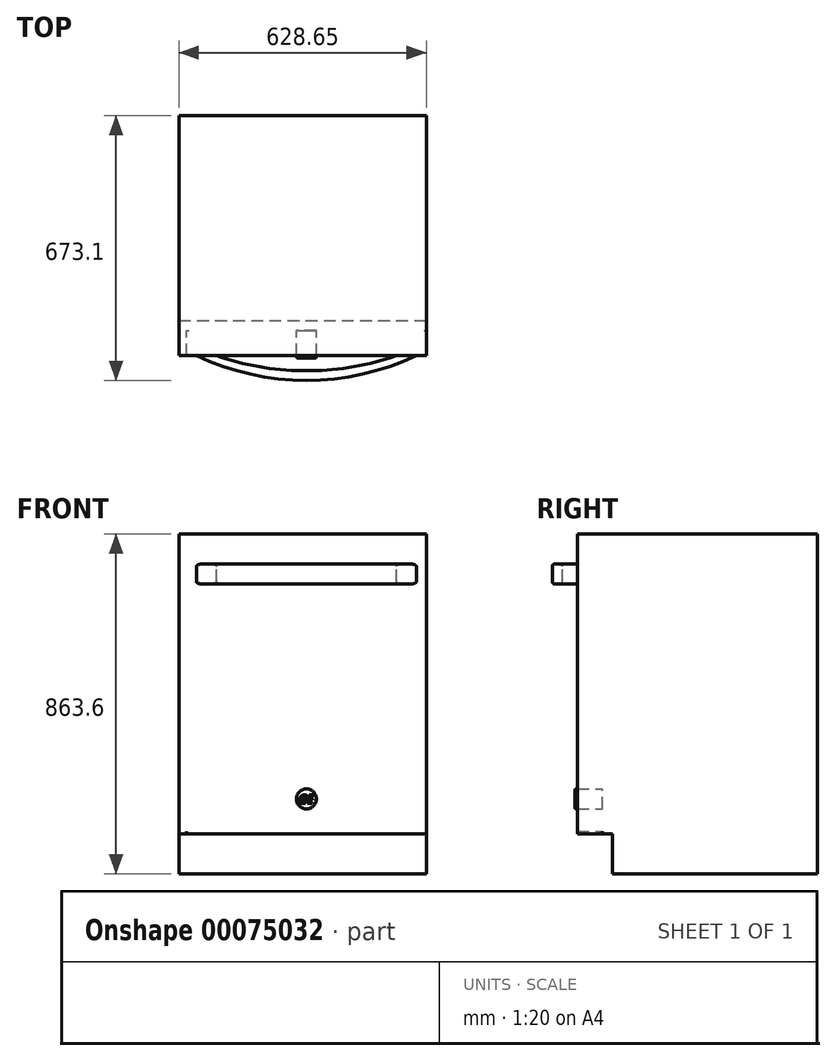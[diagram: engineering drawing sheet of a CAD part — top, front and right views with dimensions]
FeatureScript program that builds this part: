
annotation { "Feature Type Name" : "Feature", "Feature Type Description" : "" }
export const myFeature = defineFeature(function(context is Context, id is Id, definition is map)
    precondition{}
    {
        {
            var Q0;
            Q0=qCreatedBy(makeId("Front.planeOp"),FACE);
            var sketch = newSketch(context, id + "F0", { "sketchPlane" : qUnion([Q0])});
            skLineSegment(sketch, "E0.bottom", {"start": v(-304.8, 431.8) * mm, "end": v(304.8, 431.8) * mm});
            skLineSegment(sketch, "E0.top", {"start": v(-304.8, -431.8) * mm, "end": v(304.8, -431.8) * mm});
            skLineSegment(sketch, "E0.left", {"start": v(-304.8, 431.8) * mm, "end": v(-304.8, -431.8) * mm});
            skLineSegment(sketch, "E0.right", {"start": v(304.8, 431.8) * mm, "end": v(304.8, -431.8) * mm});
            skLineSegment(sketch, "E1", {"start": v(-304.8, 431.8) * mm, "end": v(304.8, -431.8) * mm, "construction": true});
            skLineSegment(sketch, "E2.bottom", {"start": v(-304.8, -330.2) * mm, "end": v(304.8, -330.2) * mm});
            skLineSegment(sketch, "E2.left", {"start": v(-304.8, -330.2) * mm, "end": v(-304.8, 431.8) * mm});
            skLineSegment(sketch, "E2.right", {"start": v(304.8, -330.2) * mm, "end": v(304.8, 431.8) * mm});
            skLineSegment(sketch, "E3", {"start": v(0, 0) * mm, "end": v(0, -330.2) * mm, "construction": true});
            skCircle(sketch, "E4", {"center": v(0, -241.3) * mm, "radius": 25.4 * mm});
            skLineSegment(sketch, "E5.bottom", {"start": v(-279.4, 355.6) * mm, "end": v(279.4, 355.6) * mm});
            skLineSegment(sketch, "E5.top", {"start": v(-279.4, 304.8) * mm, "end": v(279.4, 304.8) * mm});
            skLineSegment(sketch, "E5.left", {"start": v(-279.4, 355.6) * mm, "end": v(-279.4, 304.8) * mm});
            skLineSegment(sketch, "E5.right", {"start": v(279.4, 355.6) * mm, "end": v(279.4, 304.8) * mm});
            skLineSegment(sketch, "E6", {"start": v(0, 431.8) * mm, "end": v(0, 304.8) * mm, "construction": true});
            skSolve(sketch);
        }
        {
            var Q0;
            Q0=makeQuery(id+"F0.imprint","IMPRINT",FACE,{"disambiguationData":[TD([[makeQuery(id+"F0.imprint","IMPRINT",EDGE,{"derivedFrom":sQuery(id+"F0.wireOp",EDGE,"E2.bottom")}),1.0]])]});
            var Q1;
            Q1=makeQuery(id+"F0.imprint","IMPRINT",FACE,{"disambiguationData":[TD([[makeQuery(id+"F0.imprint","IMPRINT",EDGE,{"derivedFrom":sQuery(id+"F0.wireOp",EDGE,"E5.bottom")}),-1.0]])]});
            var Q2;
            Q2=makeQuery(id+"F0.imprint","IMPRINT",FACE,{"disambiguationData":[TD([[makeQuery(id+"F0.imprint","IMPRINT",EDGE,{"derivedFrom":sQuery(id+"F0.wireOp",EDGE,"E4")}),1.0]])]});
            var Q3;
            Q3=sQuery(id+"F0.wireOp",EDGE,"E2.right");
            var Q4;
            Q4=sQuery(id+"F0.wireOp",EDGE,"E0.bottom");
            var Q5;
            Q5=sQuery(id+"F0.wireOp",EDGE,"E2.left");
            var Q6;
            Q6=sQuery(id+"F0.wireOp",EDGE,"E2.bottom");
            extrude(context, id + "F1", {"entities" : qUnion([Q0, Q1, Q2]), "surfaceEntities" : qUnion([Q3, Q4, Q5, Q6]), "depth" : 63.5 * mm});
        }
        {
            var Q0;
            Q0=makeQuery(id+"F0.imprint","IMPRINT",FACE,{"disambiguationData":[TD([[makeQuery(id+"F0.imprint","IMPRINT",EDGE,{"derivedFrom":sQuery(id+"F0.wireOp",EDGE,"E0.top")}),1.0]])]});
            extrude(context, id + "F2", {"entities" : qUnion([Q0]), "oppositeDirection" : true, "depth" : 527.05 * mm});
        }
        {
            var Q0;
            Q0=makeQuery(id+"F0.imprint","IMPRINT",FACE,{"disambiguationData":[TD([[makeQuery(id+"F0.imprint","IMPRINT",EDGE,{"derivedFrom":sQuery(id+"F0.wireOp",EDGE,"E5.bottom")}),-1.0]])]});
            extrude(context, id + "F3", {"entities" : qUnion([Q0]), "operationType" : NewBodyOperationType.ADD, "depth" : 127 * mm});
        }
        {
            var Q0;
            Q0=makeQuery(id+"F3.opExtrude","SWEPT_FACE",FACE,{"disambiguationData":[OSD([sQuery(id+"F0.wireOp",EDGE,"E5.bottom")])]});
            var sketch = newSketch(context, id + "F4", { "sketchPlane" : qUnion([Q0])});
            skLineSegment(sketch, "E7.bottom", {"start": v(-228.6, -63.5) * mm, "end": v(228.6, -63.5) * mm});
            skLineSegment(sketch, "E7.top", {"start": v(-228.6, -101.6) * mm, "end": v(228.6, -101.6) * mm});
            skLineSegment(sketch, "E7.left", {"start": v(-228.6, -63.5) * mm, "end": v(-228.6, -101.6) * mm});
            skLineSegment(sketch, "E7.right", {"start": v(228.6, -63.5) * mm, "end": v(228.6, -101.6) * mm});
            skSolve(sketch);
        }
        {
            var Q0;
            Q0=qSketchRegion(id+"F4",true);
            extrude(context, id + "F5", {"entities" : qUnion([Q0]), "operationType" : NewBodyOperationType.REMOVE, "endBound" : BoundingType.THROUGH_ALL, "oppositeDirection" : true, "depth" : 25.4 * mm});
        }
        {
            var Q0;
            Q0=makeQuery(id+"F5.boolean.opBoolean","COPY",EDGE,{"derivedFrom":makeQuery(id+"F5.opExtrude","SWEPT_EDGE",EDGE,{"disambiguationData":[OSD([sQuery(id+"F4.wireOp",EDGE,"E7.top"),sQuery(id+"F4.wireOp",EDGE,"E7.right")])]})});
            var Q1;
            Q1=makeQuery(id+"F5.boolean.opBoolean","COPY",EDGE,{"derivedFrom":makeQuery(id+"F5.opExtrude","SWEPT_EDGE",EDGE,{"disambiguationData":[OSD([sQuery(id+"F4.wireOp",EDGE,"E7.top"),sQuery(id+"F4.wireOp",EDGE,"E7.left")])]})});
            var Q2;
            Q2=makeQuery(id+"F3.opExtrude","CAP_EDGE",EDGE,{"disambiguationData":[OSD([sQuery(id+"F0.wireOp",EDGE,"E5.left")])],"isStart":false});
            var Q3;
            Q3=makeQuery(id+"F3.opExtrude","CAP_EDGE",EDGE,{"disambiguationData":[OSD([sQuery(id+"F0.wireOp",EDGE,"E5.right")])],"isStart":false});
            fillet(context, id + "F6", {"entities" : qUnion([Q0, Q1, Q2, Q3]), "radius" : 646.43 * mm, "tangentPropagation" : true, "allowEdgeOverflow" : false});
        }
        {
            var Q0;
            Q0=makeQuery(id+"F6.opFillet","BLEND_EDGE",EDGE,{"blendedFrom":[makeQuery(id+"F3.opExtrude","CAP_EDGE",EDGE,{"disambiguationData":[OSD([sQuery(id+"F0.wireOp",EDGE,"E5.left")])],"isStart":false}),makeQuery(id+"F3.opExtrude","SWEPT_FACE",FACE,{"disambiguationData":[OSD([sQuery(id+"F0.wireOp",EDGE,"E5.bottom")])]})],"blendedInto":[makeQuery(id+"F3.opExtrude","SWEPT_FACE",FACE,{"disambiguationData":[OSD([sQuery(id+"F0.wireOp",EDGE,"E5.bottom")])]})]});
            var Q1;
            Q1=makeQuery(id+"F6.opFillet","BLEND_EDGE",EDGE,{"blendedFrom":[makeQuery(id+"F5.boolean.opBoolean","COPY",EDGE,{"derivedFrom":makeQuery(id+"F5.opExtrude","SWEPT_EDGE",EDGE,{"disambiguationData":[OSD([sQuery(id+"F4.wireOp",EDGE,"E7.top"),sQuery(id+"F4.wireOp",EDGE,"E7.right")])]})}),makeQuery(id+"F3.opExtrude","SWEPT_FACE",FACE,{"disambiguationData":[OSD([sQuery(id+"F0.wireOp",EDGE,"E5.bottom")])]})],"blendedInto":[makeQuery(id+"F3.opExtrude","SWEPT_FACE",FACE,{"disambiguationData":[OSD([sQuery(id+"F0.wireOp",EDGE,"E5.bottom")])]})]});
            var Q2;
            Q2=makeQuery(id+"F6.opFillet","BLEND_EDGE",EDGE,{"blendedFrom":[makeQuery(id+"F5.boolean.opBoolean","COPY",EDGE,{"derivedFrom":makeQuery(id+"F5.opExtrude","SWEPT_EDGE",EDGE,{"disambiguationData":[OSD([sQuery(id+"F4.wireOp",EDGE,"E7.top"),sQuery(id+"F4.wireOp",EDGE,"E7.left")])]})}),makeQuery(id+"F3.opExtrude","SWEPT_FACE",FACE,{"disambiguationData":[OSD([sQuery(id+"F0.wireOp",EDGE,"E5.bottom")])]})],"blendedInto":[makeQuery(id+"F3.opExtrude","SWEPT_FACE",FACE,{"disambiguationData":[OSD([sQuery(id+"F0.wireOp",EDGE,"E5.bottom")])]})]});
            var Q3;
            Q3=makeQuery(id+"F5.boolean.opBoolean","COPY",EDGE,{"derivedFrom":makeQuery(id+"F5.opExtrude","CAP_EDGE",EDGE,{"disambiguationData":[OSD([sQuery(id+"F4.wireOp",EDGE,"E7.top")])],"isStart":true})});
            var Q4;
            Q4=makeQuery(id+"F6.opFillet","BLEND_EDGE",EDGE,{"blendedFrom":[makeQuery(id+"F3.opExtrude","CAP_EDGE",EDGE,{"disambiguationData":[OSD([sQuery(id+"F0.wireOp",EDGE,"E5.right")])],"isStart":false}),makeQuery(id+"F3.opExtrude","SWEPT_FACE",FACE,{"disambiguationData":[OSD([sQuery(id+"F0.wireOp",EDGE,"E5.bottom")])]})],"blendedInto":[makeQuery(id+"F3.opExtrude","SWEPT_FACE",FACE,{"disambiguationData":[OSD([sQuery(id+"F0.wireOp",EDGE,"E5.bottom")])]})]});
            var Q5;
            Q5=makeQuery(id+"F6.opFillet","BLEND_EDGE",EDGE,{"blendedFrom":[makeQuery(id+"F3.opExtrude","CAP_EDGE",EDGE,{"disambiguationData":[OSD([sQuery(id+"F0.wireOp",EDGE,"E5.right")])],"isStart":false}),makeQuery(id+"F3.opExtrude","SWEPT_FACE",FACE,{"disambiguationData":[OSD([sQuery(id+"F0.wireOp",EDGE,"E5.top")])]})],"blendedInto":[makeQuery(id+"F3.opExtrude","SWEPT_FACE",FACE,{"disambiguationData":[OSD([sQuery(id+"F0.wireOp",EDGE,"E5.top")])]})]});
            var Q6;
            Q6=makeQuery(id+"F6.opFillet","BLEND_EDGE",EDGE,{"blendedFrom":[makeQuery(id+"F3.opExtrude","CAP_EDGE",EDGE,{"disambiguationData":[OSD([sQuery(id+"F0.wireOp",EDGE,"E5.left")])],"isStart":false}),makeQuery(id+"F3.opExtrude","SWEPT_FACE",FACE,{"disambiguationData":[OSD([sQuery(id+"F0.wireOp",EDGE,"E5.top")])]})],"blendedInto":[makeQuery(id+"F3.opExtrude","SWEPT_FACE",FACE,{"disambiguationData":[OSD([sQuery(id+"F0.wireOp",EDGE,"E5.top")])]})]});
            var Q7;
            Q7=makeQuery(id+"F6.opFillet","BLEND_EDGE",EDGE,{"blendedFrom":[makeQuery(id+"F5.boolean.opBoolean","COPY",EDGE,{"derivedFrom":makeQuery(id+"F5.opExtrude","SWEPT_EDGE",EDGE,{"disambiguationData":[OSD([sQuery(id+"F4.wireOp",EDGE,"E7.top"),sQuery(id+"F4.wireOp",EDGE,"E7.left")])]})}),makeQuery(id+"F3.opExtrude","SWEPT_FACE",FACE,{"disambiguationData":[OSD([sQuery(id+"F0.wireOp",EDGE,"E5.top")])]})],"blendedInto":[makeQuery(id+"F3.opExtrude","SWEPT_FACE",FACE,{"disambiguationData":[OSD([sQuery(id+"F0.wireOp",EDGE,"E5.top")])]})]});
            var Q8;
            Q8=makeQuery(id+"F6.opFillet","BLEND_EDGE",EDGE,{"blendedFrom":[makeQuery(id+"F5.boolean.opBoolean","COPY",EDGE,{"derivedFrom":makeQuery(id+"F5.opExtrude","SWEPT_EDGE",EDGE,{"disambiguationData":[OSD([sQuery(id+"F4.wireOp",EDGE,"E7.top"),sQuery(id+"F4.wireOp",EDGE,"E7.right")])]})}),makeQuery(id+"F3.opExtrude","SWEPT_FACE",FACE,{"disambiguationData":[OSD([sQuery(id+"F0.wireOp",EDGE,"E5.top")])]})],"blendedInto":[makeQuery(id+"F3.opExtrude","SWEPT_FACE",FACE,{"disambiguationData":[OSD([sQuery(id+"F0.wireOp",EDGE,"E5.top")])]})]});
            var Q9;
            Q9=makeQuery(id+"F5.boolean.opBoolean","INTERSECT",EDGE,{"derivedFrom":[makeQuery(id+"F3.opExtrude","SWEPT_FACE",FACE,{"disambiguationData":[OSD([sQuery(id+"F0.wireOp",EDGE,"E5.top")])]}),makeQuery(id+"F5.opExtrude","SWEPT_FACE",FACE,{"disambiguationData":[OSD([sQuery(id+"F4.wireOp",EDGE,"E7.top")])]})]});
            fillet(context, id + "F7", {"entities" : qUnion([Q0, Q1, Q2, Q3, Q4, Q5, Q6, Q7, Q8, Q9]), "radius" : 6.35 * mm, "tangentPropagation" : true, "allowEdgeOverflow" : false});
        }
        {
            var Q0;
            Q0=makeQuery(id+"F1.opExtrude","CAP_FACE",FACE,{"disambiguationData":[OSD([sQuery(id+"F0.wireOp",EDGE,"E2.bottom"),sQuery(id+"F0.wireOp",EDGE,"E0.bottom"),sQuery(id+"F0.wireOp",EDGE,"E2.left"),sQuery(id+"F0.wireOp",EDGE,"E2.right")])],"isStart":true});
            var Q1;
            Q1=makeQuery(id+"F2.opExtrude","CAP_FACE",FACE,{"disambiguationData":[OSD([sQuery(id+"F0.wireOp",EDGE,"E0.top"),sQuery(id+"F0.wireOp",EDGE,"E0.left"),sQuery(id+"F0.wireOp",EDGE,"E0.right"),sQuery(id+"F0.wireOp",EDGE,"E2.bottom")])],"isStart":false});
            extrude(context, id + "F8", {"entities" : qUnion([Q0]), "endBound" : BoundingType.UP_TO_SURFACE, "endBoundEntityFace" : qUnion([Q1]), "depth" : 25.4 * mm});
        }
        {
            var Q0;
            Q0=makeQuery(id+"F1.opExtrude","SWEPT_EDGE",EDGE,{"disambiguationData":[OSD([sQuery(id+"F0.wireOp",EDGE,"E0.left"),sQuery(id+"F0.wireOp",EDGE,"E2.bottom"),sQuery(id+"F0.wireOp",EDGE,"E2.left")])]});
            var Q1;
            Q1=makeQuery(id+"F1.opExtrude","SWEPT_EDGE",EDGE,{"disambiguationData":[OSD([sQuery(id+"F0.wireOp",EDGE,"E0.right"),sQuery(id+"F0.wireOp",EDGE,"E2.bottom"),sQuery(id+"F0.wireOp",EDGE,"E2.right")])]});
            fillet(context, id + "F9", {"entities" : qUnion([Q0, Q1]), "radius" : 6.35 * mm, "tangentPropagation" : true, "allowEdgeOverflow" : false});
        }
        {
            var Q0;
            Q0=makeQuery(id+"F0.imprint","IMPRINT",FACE,{"disambiguationData":[TD([[makeQuery(id+"F0.imprint","IMPRINT",EDGE,{"derivedFrom":sQuery(id+"F0.wireOp",EDGE,"E4")}),1.0]])]});
            var Q1;
            Q1=sQuery(id+"F0.wireOp",EDGE,"E4");
            extrude(context, id + "F10", {"entities" : qUnion([Q0]), "surfaceEntities" : qUnion([Q1]), "depth" : 69.85 * mm});
        }
        {
            var Q0;
            Q0=makeQuery(id+"F10.opExtrude","CAP_EDGE",EDGE,{"disambiguationData":[OSD([sQuery(id+"F0.wireOp",EDGE,"E4")])],"isStart":false});
            fillet(context, id + "F11", {"entities" : qUnion([Q0]), "radius" : 3.17 * mm, "tangentPropagation" : true, "allowEdgeOverflow" : false});
        }
        {
            var Q0;
            Q0=makeQuery(id+"F10.opExtrude","CAP_FACE",FACE,{"disambiguationData":[OSD([sQuery(id+"F0.wireOp",EDGE,"E4")])],"isStart":false});
            var sketch = newSketch(context, id + "F12", { "sketchPlane" : qUnion([Q0])});
            skText(sketch, "E8", { "text": "GE", "fontName": "OpenSans-BoldItalic.ttf"});
            const initialGuessF12  = {"E8": [-0.0191, -0.25284, 1, 0, 0.02166]};
            skSetInitialGuess(sketch, initialGuessF12);
            skSolve(sketch);
        }
        {
            var Q0;
            Q0=qSketchRegion(id+"F12",true);
            extrude(context, id + "F13", {"entities" : qUnion([Q0]), "operationType" : NewBodyOperationType.REMOVE, "oppositeDirection" : true, "depth" : 3.17 * mm});
        }
        {
            var Q0;
            Q0=makeQuery(id+"F2.opExtrude","CAP_FACE",FACE,{"disambiguationData":[OSD([sQuery(id+"F0.wireOp",EDGE,"E0.top"),sQuery(id+"F0.wireOp",EDGE,"E0.left"),sQuery(id+"F0.wireOp",EDGE,"E0.right"),sQuery(id+"F0.wireOp",EDGE,"E2.bottom")])],"isStart":true});
            extrude(context, id + "F14", {"entities" : qUnion([Q0]), "operationType" : NewBodyOperationType.REMOVE, "oppositeDirection" : true, "depth" : 25.4 * mm});
        }
        {
            var Q0;
            Q0=makeQuery(id+"F8.opExtrude","CAP_FACE",FACE,{"disambiguationData":[OSD([sQuery(id+"F0.wireOp",EDGE,"E2.bottom"),sQuery(id+"F0.wireOp",EDGE,"E0.bottom"),sQuery(id+"F0.wireOp",EDGE,"E2.left"),sQuery(id+"F0.wireOp",EDGE,"E2.right")])],"isStart":false});
            var sketch = newSketch(context, id + "F15", { "sketchPlane" : qUnion([Q0])});
            skLineSegment(sketch, "E9.bottom", {"start": v(304.8, 431.8) * mm, "end": v(-304.8, 431.8) * mm});
            skLineSegment(sketch, "E9.top", {"start": v(304.8, -431.8) * mm, "end": v(-304.8, -431.8) * mm});
            skLineSegment(sketch, "E9.left", {"start": v(304.8, 431.8) * mm, "end": v(304.8, -431.8) * mm});
            skLineSegment(sketch, "E9.right", {"start": v(-304.8, 431.8) * mm, "end": v(-304.8, -431.8) * mm});
            skSolve(sketch);
        }
        {
            var Q0;
            Q0=qSketchRegion(id+"F15",true);
            extrude(context, id + "F16", {"entities" : qUnion([Q0]), "depth" : 19.05 * mm});
        }
        {
            var Q0;
            Q0=makeQuery(id+"F16.opExtrude","SWEPT_FACE",FACE,{"disambiguationData":[OSD([sQuery(id+"F15.wireOp",EDGE,"E9.left")])]});
            var sketch = newSketch(context, id + "F17", { "sketchPlane" : qUnion([Q0])});
            skLineSegment(sketch, "E10.bottom", {"start": v(-546.1, 431.8) * mm, "end": v(63.5, 431.8) * mm});
            skLineSegment(sketch, "E10.top", {"start": v(-546.1, -431.8) * mm, "end": v(-25.4, -431.8) * mm});
            skLineSegment(sketch, "E10.left", {"start": v(-546.1, 431.8) * mm, "end": v(-546.1, -431.8) * mm});
            skLineSegment(sketch, "E10.right", {"start": v(63.5, 431.8) * mm, "end": v(63.5, -330.2) * mm});
            skLineSegment(sketch, "E11", {"start": v(-25.4, -431.8) * mm, "end": v(-25.4, -330.2) * mm});
            skLineSegment(sketch, "E12", {"start": v(63.5, -330.2) * mm, "end": v(-25.4, -330.2) * mm});
            skSolve(sketch);
        }
        {
            var Q0;
            Q0 = qSketchRegion(id + "F17", true);
            extrude(context, id + "F18", {"entities" : qUnion([Q0]), "operationType" : NewBodyOperationType.ADD, "depth" : 19.05 * mm});
        }
    });
